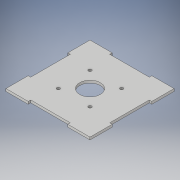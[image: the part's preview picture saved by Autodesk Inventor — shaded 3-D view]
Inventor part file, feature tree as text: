
AUTODESK INVENTOR PART (.ipt)
format: ipt  version: 2019 (Build 230136000, 136)  size: 134,656 bytes
history: native  units: mm
features: extrude x1, sketch x1
ambient origin geometry x8: Origin, YZ Plane, XZ Plane, XY Plane, X Axis, Y Axis, Z Axis, Center Point
bodies: Body1 (feature_tree)
feature tree (2):
  extrude  "Extrusión2"  Depth=106.36mm
  sketch  "Boceto1"  dims[d0=26.0mm d1=106.36mm d2=106.36mm d3=3.18mm d4=50.0mm d5=25.0mm d6=25.0mm d9=4.0mm d10=4.0mm d11=4.0mm d12=4.0mm d13=20.0mm d14=20.0mm d15=40.0mm d16=20.0mm d17=40.0mm d18=40.0mm d19=40.0mm d20=3.18mm d21=0.0mm]
